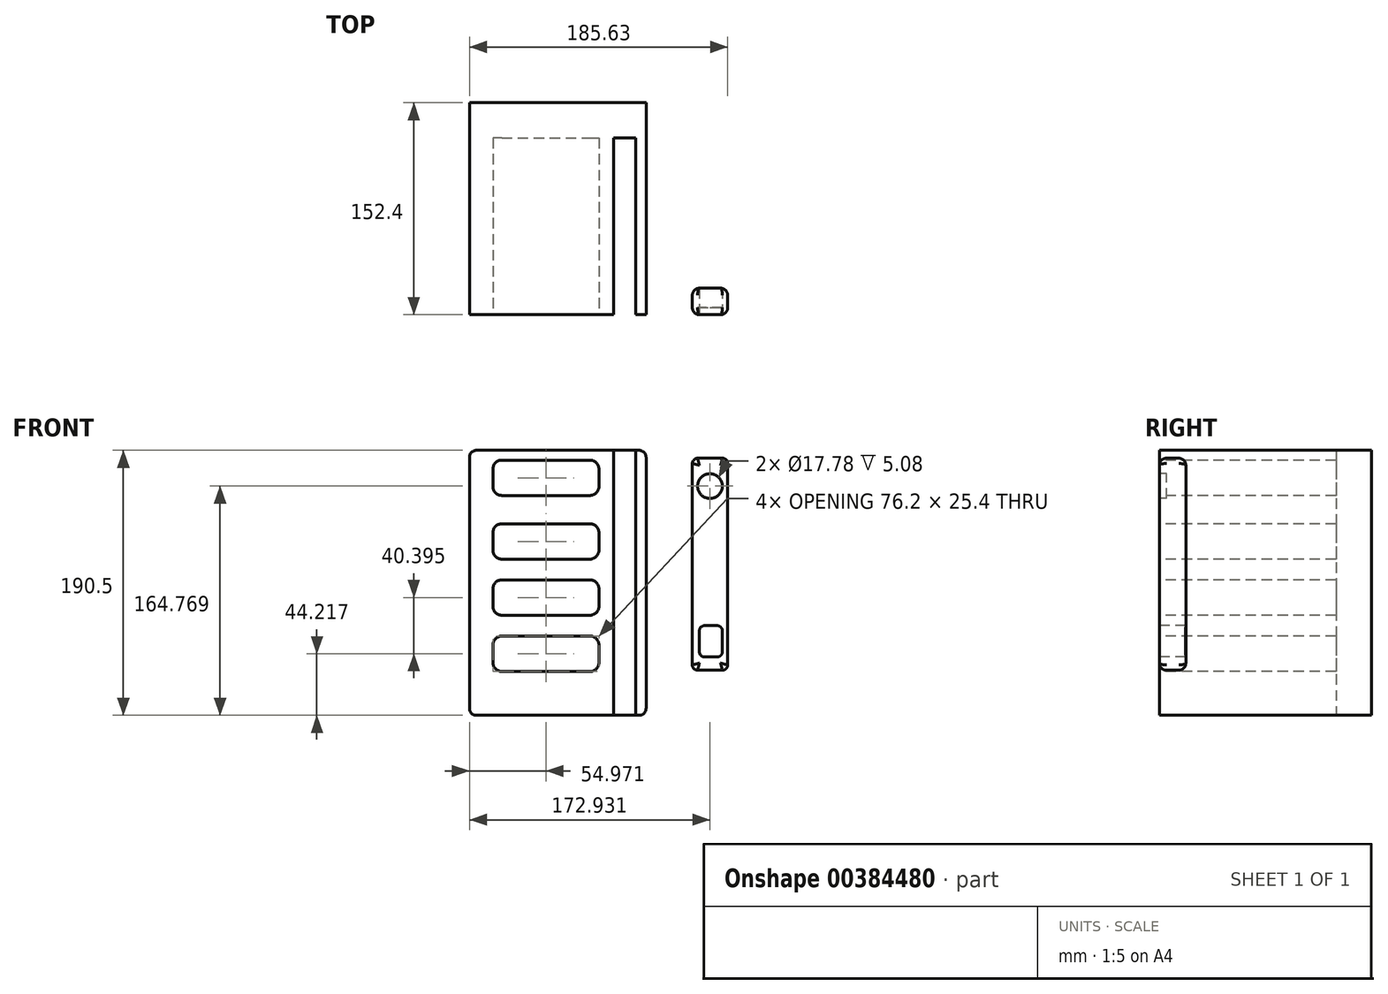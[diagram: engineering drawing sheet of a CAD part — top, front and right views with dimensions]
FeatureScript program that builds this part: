
annotation { "Feature Type Name" : "Feature", "Feature Type Description" : "" }
export const myFeature = defineFeature(function(context is Context, id is Id, definition is map)
    precondition{}
    {
        {
            var Q0;
            Q0=qCreatedBy(makeId("Front.planeOp"),FACE);
            var sketch = newSketch(context, id + "F0", { "sketchPlane" : qUnion([Q0])});
            skLineSegment(sketch, "E0.bottom", {"start": v(-104.14, 137.66) * mm, "end": v(12.7, 137.66) * mm});
            skLineSegment(sketch, "E0.top", {"start": v(-104.14, -52.84) * mm, "end": v(12.7, -52.84) * mm});
            skLineSegment(sketch, "E0.left", {"start": v(-109.22, 132.58) * mm, "end": v(-109.22, -47.76) * mm});
            skLineSegment(sketch, "E0.right", {"start": v(17.78, 132.58) * mm, "end": v(17.78, -47.76) * mm});
            skPoint(sketch, "E1.visualSharp", {"position": v(-109.22, 137.66) * mm});
            skArc(sketch, "E1.filletArc", {"start": v(-104.14, 137.66) * mm, "mid": v(-107.73, 136.17) * mm, "end": v(-109.22, 132.58) * mm});
            skPoint(sketch, "E2.visualSharp", {"position": v(17.78, 137.66) * mm});
            skArc(sketch, "E2.filletArc", {"start": v(17.78, 132.58) * mm, "mid": v(16.3, 136.17) * mm, "end": v(12.7, 137.66) * mm});
            skPoint(sketch, "E3.visualSharp", {"position": v(-109.22, -52.84) * mm});
            skArc(sketch, "E3.filletArc", {"start": v(-109.22, -47.76) * mm, "mid": v(-107.73, -51.35) * mm, "end": v(-104.14, -52.84) * mm});
            skPoint(sketch, "E4.visualSharp", {"position": v(17.78, -52.84) * mm});
            skArc(sketch, "E4.filletArc", {"start": v(12.7, -52.84) * mm, "mid": v(16.3, -51.35) * mm, "end": v(17.78, -47.76) * mm});
            skSolve(sketch);
        }
        {
            var Q0;
            Q0=qCreatedBy(makeId("Front.planeOp"),FACE);
            var sketch = newSketch(context, id + "F1", { "sketchPlane" : qUnion([Q0])});
            skLineSegment(sketch, "E5.bottom", {"start": v(-86, 130.6) * mm, "end": v(-22.5, 130.6) * mm});
            skLineSegment(sketch, "E5.top", {"start": v(-86, 105.2) * mm, "end": v(-22.5, 105.2) * mm});
            skLineSegment(sketch, "E5.left", {"start": v(-92.35, 124.25) * mm, "end": v(-92.35, 111.55) * mm});
            skLineSegment(sketch, "E5.right", {"start": v(-16.15, 124.25) * mm, "end": v(-16.15, 111.55) * mm});
            skLineSegment(sketch, "E6.bottom", {"start": v(-86, 84.87) * mm, "end": v(-22.5, 84.87) * mm});
            skLineSegment(sketch, "E6.top", {"start": v(-86, 59.47) * mm, "end": v(-22.5, 59.47) * mm});
            skLineSegment(sketch, "E6.left", {"start": v(-92.35, 78.52) * mm, "end": v(-92.35, 65.82) * mm});
            skLineSegment(sketch, "E6.right", {"start": v(-16.15, 78.52) * mm, "end": v(-16.15, 65.82) * mm});
            skLineSegment(sketch, "E7.bottom", {"start": v(-86, 44.47) * mm, "end": v(-22.5, 44.47) * mm});
            skLineSegment(sketch, "E7.top", {"start": v(-86, 19.07) * mm, "end": v(-22.5, 19.07) * mm});
            skLineSegment(sketch, "E7.left", {"start": v(-92.35, 38.12) * mm, "end": v(-92.35, 25.42) * mm});
            skLineSegment(sketch, "E7.right", {"start": v(-16.15, 38.12) * mm, "end": v(-16.15, 25.42) * mm});
            skLineSegment(sketch, "E8.bottom", {"start": v(-86, 4.08) * mm, "end": v(-22.5, 4.08) * mm});
            skLineSegment(sketch, "E8.top", {"start": v(-86, -21.32) * mm, "end": v(-22.5, -21.32) * mm});
            skLineSegment(sketch, "E8.left", {"start": v(-92.35, -2.27) * mm, "end": v(-92.35, -14.97) * mm});
            skLineSegment(sketch, "E8.right", {"start": v(-16.15, -2.27) * mm, "end": v(-16.15, -14.97) * mm});
            skLineSegment(sketch, "E9.bottom", {"start": v(-5.46, 138.93) * mm, "end": v(10.16, 138.93) * mm});
            skLineSegment(sketch, "E9.top", {"start": v(-5.46, -52.84) * mm, "end": v(10.16, -52.84) * mm});
            skLineSegment(sketch, "E9.left", {"start": v(-5.46, 138.93) * mm, "end": v(-5.46, -52.84) * mm});
            skLineSegment(sketch, "E9.right", {"start": v(10.16, 138.93) * mm, "end": v(10.16, -52.84) * mm});
            skPoint(sketch, "E10.visualSharp", {"position": v(-92.35, 130.6) * mm});
            skArc(sketch, "E10.filletArc", {"start": v(-86, 130.6) * mm, "mid": v(-90.49, 128.74) * mm, "end": v(-92.35, 124.25) * mm});
            skPoint(sketch, "E11.visualSharp", {"position": v(-16.15, 130.6) * mm});
            skArc(sketch, "E11.filletArc", {"start": v(-16.15, 124.25) * mm, "mid": v(-18, 128.74) * mm, "end": v(-22.5, 130.6) * mm});
            skPoint(sketch, "E12.visualSharp", {"position": v(-92.35, 105.2) * mm});
            skArc(sketch, "E12.filletArc", {"start": v(-92.35, 111.55) * mm, "mid": v(-90.49, 107.06) * mm, "end": v(-86, 105.2) * mm});
            skPoint(sketch, "E13.visualSharp", {"position": v(-16.15, 105.2) * mm});
            skArc(sketch, "E13.filletArc", {"start": v(-22.5, 105.2) * mm, "mid": v(-18, 107.06) * mm, "end": v(-16.15, 111.55) * mm});
            skPoint(sketch, "E14.visualSharp", {"position": v(-16.15, 84.87) * mm});
            skArc(sketch, "E14.filletArc", {"start": v(-16.15, 78.52) * mm, "mid": v(-18, 83) * mm, "end": v(-22.5, 84.87) * mm});
            skPoint(sketch, "E15.visualSharp", {"position": v(-92.35, 84.87) * mm});
            skArc(sketch, "E15.filletArc", {"start": v(-86, 84.87) * mm, "mid": v(-90.49, 83) * mm, "end": v(-92.35, 78.52) * mm});
            skPoint(sketch, "E16.visualSharp", {"position": v(-92.35, 59.47) * mm});
            skArc(sketch, "E16.filletArc", {"start": v(-92.35, 65.82) * mm, "mid": v(-90.49, 61.33) * mm, "end": v(-86, 59.47) * mm});
            skPoint(sketch, "E17.visualSharp", {"position": v(-16.15, 59.47) * mm});
            skArc(sketch, "E17.filletArc", {"start": v(-22.5, 59.47) * mm, "mid": v(-18, 61.33) * mm, "end": v(-16.15, 65.82) * mm});
            skPoint(sketch, "E18.visualSharp", {"position": v(-92.35, 44.47) * mm});
            skArc(sketch, "E18.filletArc", {"start": v(-86, 44.47) * mm, "mid": v(-90.49, 42.61) * mm, "end": v(-92.35, 38.12) * mm});
            skPoint(sketch, "E19.visualSharp", {"position": v(-16.15, 44.47) * mm});
            skArc(sketch, "E19.filletArc", {"start": v(-16.15, 38.12) * mm, "mid": v(-18, 42.61) * mm, "end": v(-22.5, 44.47) * mm});
            skPoint(sketch, "E20.visualSharp", {"position": v(-92.35, 19.07) * mm});
            skArc(sketch, "E20.filletArc", {"start": v(-92.35, 25.42) * mm, "mid": v(-90.49, 20.93) * mm, "end": v(-86, 19.07) * mm});
            skPoint(sketch, "E21.visualSharp", {"position": v(-16.15, 19.07) * mm});
            skArc(sketch, "E21.filletArc", {"start": v(-22.5, 19.07) * mm, "mid": v(-18, 20.93) * mm, "end": v(-16.15, 25.42) * mm});
            skPoint(sketch, "E22.visualSharp", {"position": v(-16.15, 4.08) * mm});
            skArc(sketch, "E22.filletArc", {"start": v(-16.15, -2.27) * mm, "mid": v(-18, 2.22) * mm, "end": v(-22.5, 4.08) * mm});
            skPoint(sketch, "E23.visualSharp", {"position": v(-92.35, 4.08) * mm});
            skArc(sketch, "E23.filletArc", {"start": v(-86, 4.08) * mm, "mid": v(-90.49, 2.22) * mm, "end": v(-92.35, -2.27) * mm});
            skPoint(sketch, "E24.visualSharp", {"position": v(-92.35, -21.32) * mm});
            skArc(sketch, "E24.filletArc", {"start": v(-92.35, -14.97) * mm, "mid": v(-90.49, -19.46) * mm, "end": v(-86, -21.32) * mm});
            skPoint(sketch, "E25.visualSharp", {"position": v(-16.15, -21.32) * mm});
            skArc(sketch, "E25.filletArc", {"start": v(-22.5, -21.32) * mm, "mid": v(-18, -19.46) * mm, "end": v(-16.15, -14.97) * mm});
            skSolve(sketch);
        }
        {
            var Q0;
            Q0=makeQuery(id+"F0.imprint","IMPRINT",FACE,{"disambiguationData":[TD([[makeQuery(id+"F0.imprint","IMPRINT",EDGE,{"derivedFrom":sQuery(id+"F0.wireOp",EDGE,"E0.bottom")}),-1.0]])]});
            extrude(context, id + "F2", {"entities" : qUnion([Q0]), "oppositeDirection" : true, "depth" : 152.4 * mm});
        }
        {
            var Q0;
            Q0=makeQuery(id+"F1.imprint","IMPRINT",FACE,{"disambiguationData":[TD([[makeQuery(id+"F1.imprint","IMPRINT",EDGE,{"derivedFrom":sQuery(id+"F1.wireOp",EDGE,"E5.bottom")}),-1.0]])]});
            var Q1;
            Q1=makeQuery(id+"F1.imprint","IMPRINT",FACE,{"disambiguationData":[TD([[makeQuery(id+"F1.imprint","IMPRINT",EDGE,{"derivedFrom":sQuery(id+"F1.wireOp",EDGE,"E6.bottom")}),-1.0]])]});
            var Q2;
            Q2=makeQuery(id+"F1.imprint","IMPRINT",FACE,{"disambiguationData":[TD([[makeQuery(id+"F1.imprint","IMPRINT",EDGE,{"derivedFrom":sQuery(id+"F1.wireOp",EDGE,"E7.bottom")}),-1.0]])]});
            var Q3;
            Q3=makeQuery(id+"F1.imprint","IMPRINT",FACE,{"disambiguationData":[TD([[makeQuery(id+"F1.imprint","IMPRINT",EDGE,{"derivedFrom":sQuery(id+"F1.wireOp",EDGE,"E8.bottom")}),-1.0]])]});
            var Q4;
            Q4=makeQuery(id+"F1.imprint","IMPRINT",FACE,{"disambiguationData":[TD([[makeQuery(id+"F1.imprint","IMPRINT",EDGE,{"derivedFrom":sQuery(id+"F1.wireOp",EDGE,"E9.bottom")}),-1.0]])]});
            extrude(context, id + "F3", {"entities" : qUnion([Q0, Q1, Q2, Q3, Q4]), "operationType" : NewBodyOperationType.REMOVE, "oppositeDirection" : true, "depth" : 127 * mm});
        }
        {
            var Q0;
            Q0=qCreatedBy(makeId("Front.planeOp"),FACE);
            var sketch = newSketch(context, id + "F4", { "sketchPlane" : qUnion([Q0])});
            skLineSegment(sketch, "E26.bottom", {"start": v(54.82, 131.99) * mm, "end": v(72.6, 131.99) * mm});
            skLineSegment(sketch, "E26.top", {"start": v(54.82, -20.41) * mm, "end": v(72.6, -20.41) * mm});
            skLineSegment(sketch, "E26.left", {"start": v(51.01, 128.18) * mm, "end": v(51.01, -16.6) * mm});
            skLineSegment(sketch, "E26.right", {"start": v(76.41, 128.18) * mm, "end": v(76.41, -16.6) * mm});
            skPoint(sketch, "E27.visualSharp", {"position": v(51.01, 131.99) * mm});
            skArc(sketch, "E27.filletArc", {"start": v(54.82, 131.99) * mm, "mid": v(52.13, 130.87) * mm, "end": v(51.01, 128.18) * mm});
            skPoint(sketch, "E28.visualSharp", {"position": v(76.41, 131.99) * mm});
            skArc(sketch, "E28.filletArc", {"start": v(76.41, 128.18) * mm, "mid": v(75.3, 130.87) * mm, "end": v(72.6, 131.99) * mm});
            skPoint(sketch, "E29.visualSharp", {"position": v(76.41, -20.41) * mm});
            skArc(sketch, "E29.filletArc", {"start": v(72.6, -20.41) * mm, "mid": v(75.3, -19.3) * mm, "end": v(76.41, -16.6) * mm});
            skPoint(sketch, "E30.visualSharp", {"position": v(51.01, -20.41) * mm});
            skArc(sketch, "E30.filletArc", {"start": v(51.01, -16.6) * mm, "mid": v(52.13, -19.3) * mm, "end": v(54.82, -20.41) * mm});
            skLineSegment(sketch, "E31.bottom", {"start": v(59.9, 11.64) * mm, "end": v(68.8, 11.64) * mm});
            skLineSegment(sketch, "E31.top", {"start": v(59.9, -10.96) * mm, "end": v(68.8, -10.96) * mm});
            skLineSegment(sketch, "E31.left", {"start": v(56.08, 7.83) * mm, "end": v(56.08, -7.15) * mm});
            skLineSegment(sketch, "E31.right", {"start": v(72.6, 7.83) * mm, "end": v(72.6, -7.15) * mm});
            skPoint(sketch, "E32.visualSharp", {"position": v(56.08, 11.64) * mm});
            skArc(sketch, "E32.filletArc", {"start": v(59.9, 11.64) * mm, "mid": v(57.2, 10.53) * mm, "end": v(56.08, 7.83) * mm});
            skPoint(sketch, "E33.visualSharp", {"position": v(72.6, 11.64) * mm});
            skArc(sketch, "E33.filletArc", {"start": v(72.6, 7.83) * mm, "mid": v(71.49, 10.53) * mm, "end": v(68.8, 11.64) * mm});
            skPoint(sketch, "E34.visualSharp", {"position": v(72.6, -10.96) * mm});
            skArc(sketch, "E34.filletArc", {"start": v(68.8, -10.96) * mm, "mid": v(71.49, -9.85) * mm, "end": v(72.6, -7.15) * mm});
            skPoint(sketch, "E35.visualSharp", {"position": v(56.08, -10.96) * mm});
            skArc(sketch, "E35.filletArc", {"start": v(56.08, -7.15) * mm, "mid": v(57.2, -9.85) * mm, "end": v(59.9, -10.96) * mm});
            skCircle(sketch, "E36", {"center": v(63.71, 111.93) * mm, "radius": 8.9 * mm});
            skPoint(sketch, "E36.centerSnap0", {"position": v(63.71, 131.99) * mm});
            skSolve(sketch);
        }
        {
            var Q0;
            Q0=makeQuery(id+"F4.imprint","IMPRINT",FACE,{"disambiguationData":[TD([[makeQuery(id+"F4.imprint","IMPRINT",EDGE,{"derivedFrom":sQuery(id+"F4.wireOp",EDGE,"E26.bottom")}),-1.0]])]});
            var Q1;
            Q1=makeQuery(id+"F4.imprint","IMPRINT",FACE,{"disambiguationData":[TD([[makeQuery(id+"F4.imprint","IMPRINT",EDGE,{"derivedFrom":sQuery(id+"F4.wireOp",EDGE,"E36")}),1.0]])]});
            extrude(context, id + "F5", {"entities" : qUnion([Q0, Q1]), "oppositeDirection" : true, "depth" : 19.05 * mm});
        }
        {
            var Q0;
            Q0=makeQuery(id+"F4.imprint","IMPRINT",FACE,{"disambiguationData":[TD([[makeQuery(id+"F4.imprint","IMPRINT",EDGE,{"derivedFrom":sQuery(id+"F4.wireOp",EDGE,"E36")}),1.0]])]});
            extrude(context, id + "F6", {"entities" : qUnion([Q0]), "operationType" : NewBodyOperationType.REMOVE, "oppositeDirection" : true, "depth" : 5.08 * mm});
        }
        {
            var Q0;
            Q0=makeQuery(id+"F5.opExtrude","CAP_EDGE",EDGE,{"disambiguationData":[OSD([sQuery(id+"F4.wireOp",EDGE,"E26.right")])],"isStart":false});
            var Q1;
            Q1=makeQuery(id+"F5.opExtrude","CAP_EDGE",EDGE,{"disambiguationData":[OSD([sQuery(id+"F4.wireOp",EDGE,"E26.right")])],"isStart":true});
            fillet(context, id + "F7", {"entities" : qUnion([Q0, Q1]), "radius" : 5.08 * mm, "tangentPropagation" : true, "allowEdgeOverflow" : false});
        }
    });
